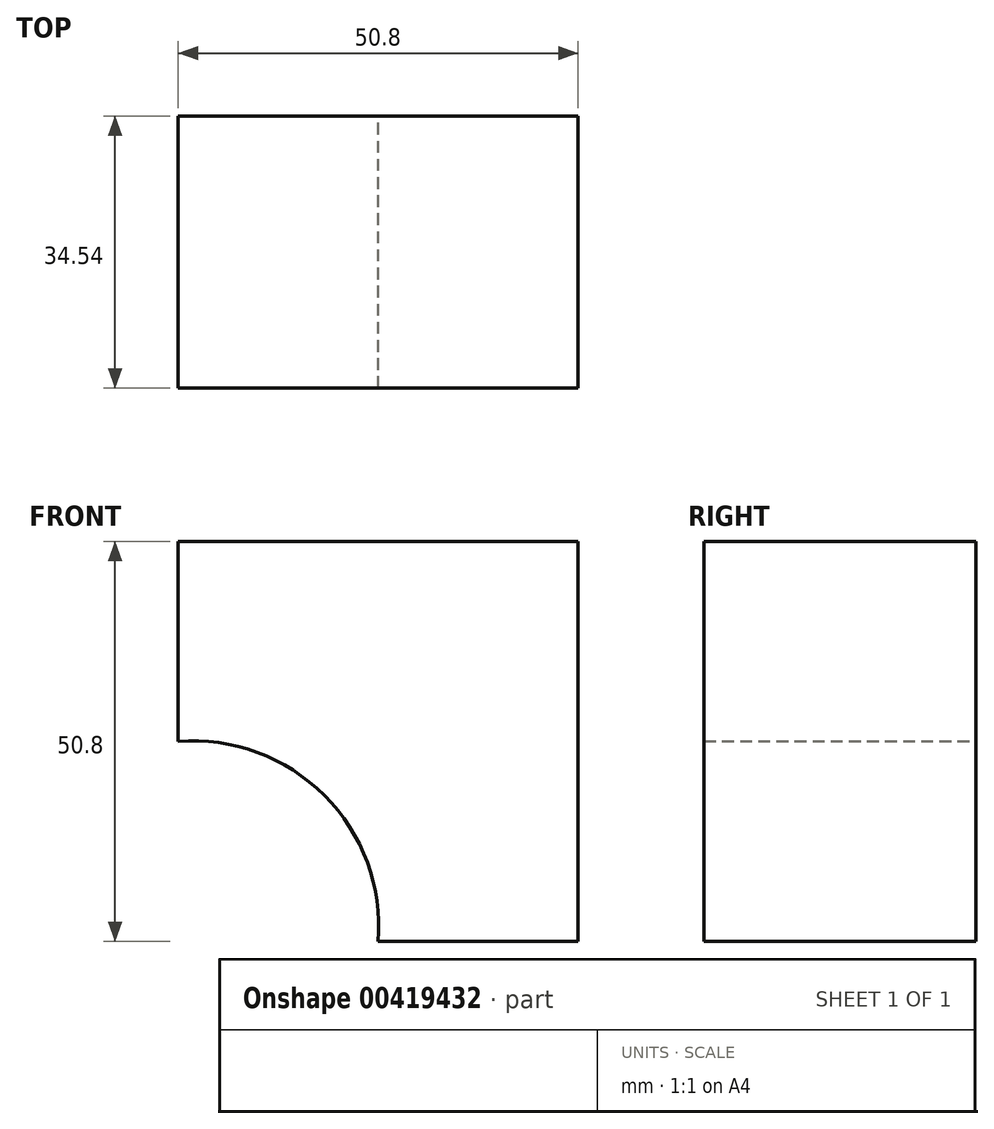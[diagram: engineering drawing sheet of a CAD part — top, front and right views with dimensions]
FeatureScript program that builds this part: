
annotation { "Feature Type Name" : "Feature", "Feature Type Description" : "" }
export const myFeature = defineFeature(function(context is Context, id is Id, definition is map)
    precondition{}
    {
        {
            var Q0;
            Q0=qCreatedBy(makeId("Front.planeOp"),FACE);
            var sketch = newSketch(context, id + "F0", { "sketchPlane" : qUnion([Q0])});
            skLineSegment(sketch, "E0.bottom", {"start": v(0, 0) * mm, "end": v(-25.4, 0) * mm});
            skLineSegment(sketch, "E0.top", {"start": v(0, 50.8) * mm, "end": v(-50.8, 50.8) * mm});
            skLineSegment(sketch, "E0.left", {"start": v(0, 0) * mm, "end": v(0, 50.8) * mm});
            skLineSegment(sketch, "E0.right", {"start": v(-50.8, 25.4) * mm, "end": v(-50.8, 50.8) * mm});
            skArc(sketch, "E1", {"start": v(-25.4, 0) * mm, "mid": v(-32.24, 18.56) * mm, "end": v(-50.8, 25.4) * mm});
            skPoint(sketch, "E2.orphan", {"position": v(-50.8, 0) * mm});
            skSolve(sketch);
        }
        {
            var Q0;
            Q0 = qSketchRegion(id + "F0", true);
            extrude(context, id + "F1", {"entities" : qUnion([Q0]), "depth" : 34.54 * mm});
        }
    });
